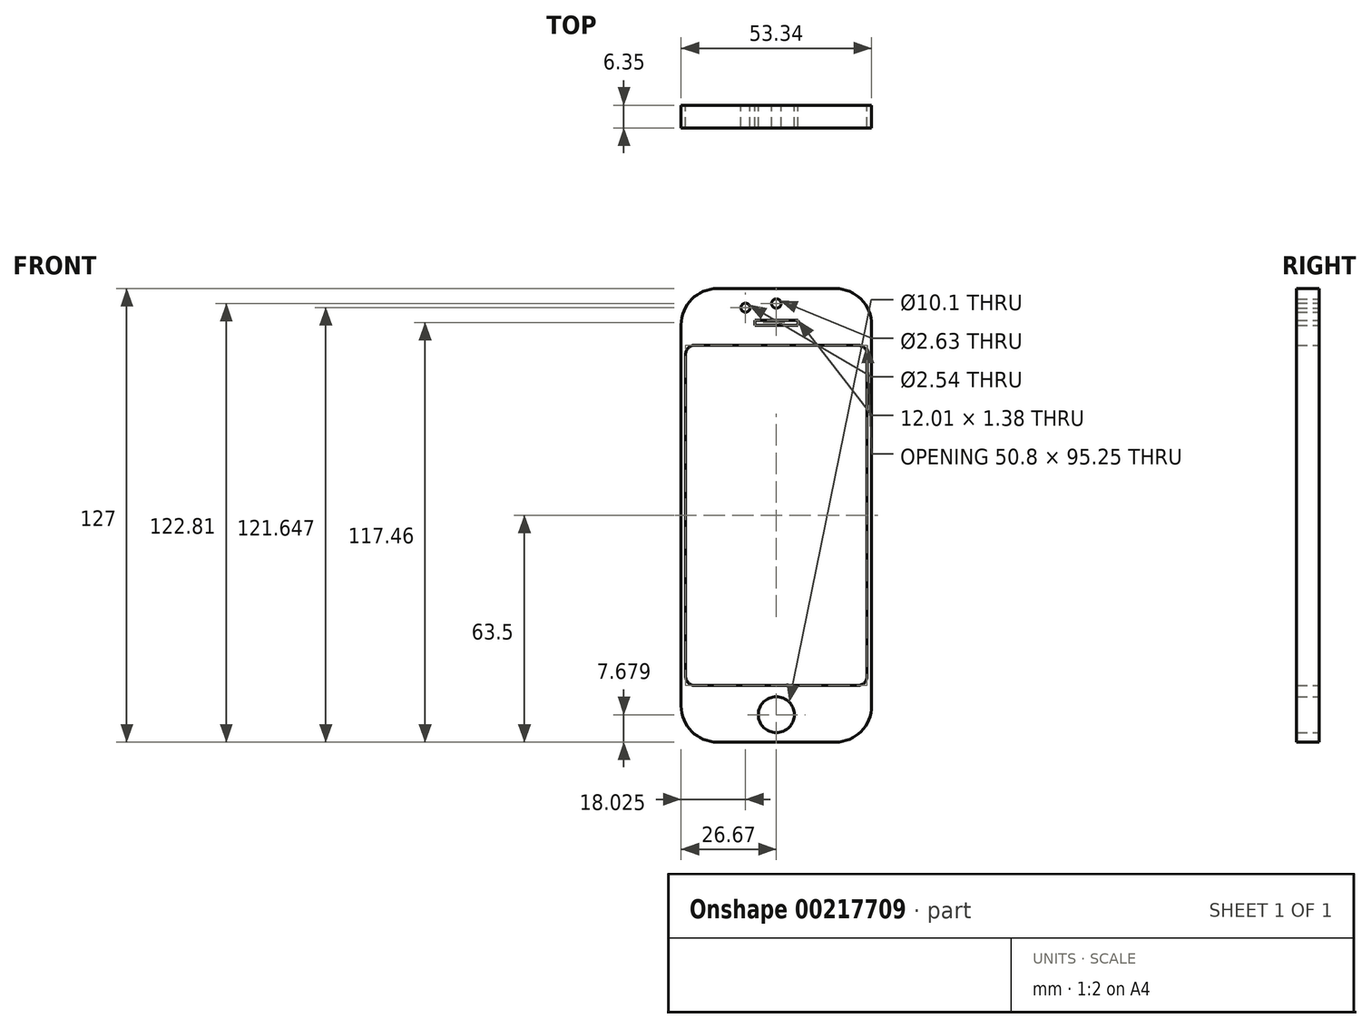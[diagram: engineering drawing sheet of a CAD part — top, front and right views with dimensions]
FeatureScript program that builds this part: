
annotation { "Feature Type Name" : "Feature", "Feature Type Description" : "" }
export const myFeature = defineFeature(function(context is Context, id is Id, definition is map)
    precondition{}
    {
        {
            var Q0;
            Q0=qCreatedBy(makeId("Front.planeOp"),FACE);
            var sketch = newSketch(context, id + "F0", { "sketchPlane" : qUnion([Q0])});
            skLineSegment(sketch, "E0.bottom", {"start": v(-16.51, -63.5) * mm, "end": v(16.51, -63.5) * mm});
            skLineSegment(sketch, "E0.top", {"start": v(-16.51, 63.5) * mm, "end": v(16.51, 63.5) * mm});
            skLineSegment(sketch, "E0.left", {"start": v(-26.67, -53.34) * mm, "end": v(-26.67, 53.34) * mm});
            skLineSegment(sketch, "E0.right", {"start": v(26.67, -53.34) * mm, "end": v(26.67, 53.34) * mm});
            skPoint(sketch, "E0.middle", {"position": v(0, 0) * mm});
            skCircle(sketch, "E1", {"center": v(0, -55.82) * mm, "radius": 5.05 * mm});
            skPoint(sketch, "E2.visualSharp", {"position": v(-26.67, -63.5) * mm});
            skArc(sketch, "E2.filletArc", {"start": v(-26.67, -53.34) * mm, "mid": v(-23.7, -60.52) * mm, "end": v(-16.51, -63.5) * mm});
            skPoint(sketch, "E3.visualSharp", {"position": v(26.67, -63.5) * mm});
            skArc(sketch, "E3.filletArc", {"start": v(16.51, -63.5) * mm, "mid": v(23.7, -60.52) * mm, "end": v(26.67, -53.34) * mm});
            skPoint(sketch, "E4.visualSharp", {"position": v(26.67, 63.5) * mm});
            skArc(sketch, "E4.filletArc", {"start": v(26.67, 53.34) * mm, "mid": v(23.7, 60.52) * mm, "end": v(16.51, 63.5) * mm});
            skPoint(sketch, "E5.visualSharp", {"position": v(-26.67, 63.5) * mm});
            skArc(sketch, "E5.filletArc", {"start": v(-16.51, 63.5) * mm, "mid": v(-23.7, 60.52) * mm, "end": v(-26.67, 53.34) * mm});
            skLineSegment(sketch, "E6.bottom", {"start": v(-22.86, -47.63) * mm, "end": v(22.86, -47.63) * mm});
            skLineSegment(sketch, "E6.top", {"start": v(-22.86, 47.63) * mm, "end": v(22.86, 47.63) * mm});
            skLineSegment(sketch, "E6.left", {"start": v(-25.4, -45.09) * mm, "end": v(-25.4, 45.09) * mm});
            skLineSegment(sketch, "E6.right", {"start": v(25.4, -45.09) * mm, "end": v(25.4, 45.09) * mm});
            skCircle(sketch, "E7", {"center": v(0, 59.3) * mm, "radius": 1.32 * mm});
            skCircle(sketch, "E8", {"center": v(-8.65, 58.15) * mm, "radius": 1.27 * mm});
            skLineSegment(sketch, "E9.bottom", {"start": v(-6, 53.27) * mm, "end": v(6, 53.27) * mm});
            skLineSegment(sketch, "E9.top", {"start": v(-6, 54.65) * mm, "end": v(6, 54.65) * mm});
            skLineSegment(sketch, "E9.left", {"start": v(-6, 53.27) * mm, "end": v(-6, 54.65) * mm});
            skLineSegment(sketch, "E9.right", {"start": v(6, 53.27) * mm, "end": v(6, 54.65) * mm});
            skPoint(sketch, "E9.middle", {"position": v(0, 53.96) * mm});
            skPoint(sketch, "E10.visualSharp", {"position": v(-25.4, -47.63) * mm});
            skArc(sketch, "E10.filletArc", {"start": v(-25.4, -45.09) * mm, "mid": v(-24.66, -46.88) * mm, "end": v(-22.86, -47.63) * mm});
            skPoint(sketch, "E11.visualSharp", {"position": v(-25.4, 47.63) * mm});
            skArc(sketch, "E11.filletArc", {"start": v(-22.86, 47.63) * mm, "mid": v(-24.66, 46.88) * mm, "end": v(-25.4, 45.09) * mm});
            skPoint(sketch, "E12.visualSharp", {"position": v(25.4, 47.63) * mm});
            skArc(sketch, "E12.filletArc", {"start": v(25.4, 45.09) * mm, "mid": v(24.66, 46.88) * mm, "end": v(22.86, 47.62) * mm});
            skPoint(sketch, "E13.visualSharp", {"position": v(25.4, -47.63) * mm});
            skArc(sketch, "E13.filletArc", {"start": v(22.86, -47.63) * mm, "mid": v(24.66, -46.88) * mm, "end": v(25.4, -45.09) * mm});
            skPoint(sketch, "E14", {"position": v(0, 63.5) * mm});
            skSolve(sketch);
        }
        {
            var Q0;
            Q0 = qSketchRegion(id + "F0", true);
            extrude(context, id + "F1", {"entities" : qUnion([Q0]), "depth" : 6.35 * mm, "offsetDistance" : 25.4 * mm});
        }
    });
